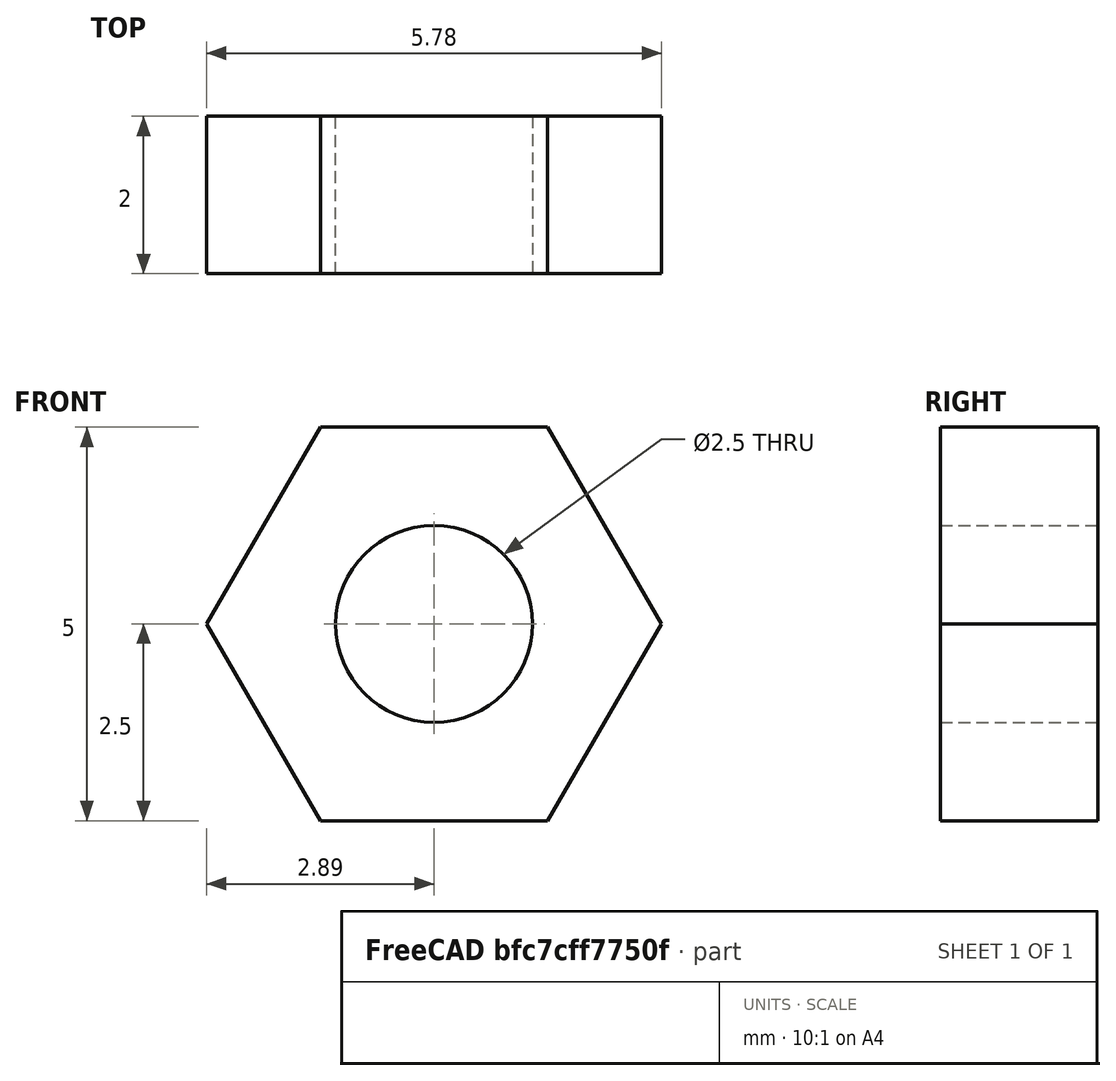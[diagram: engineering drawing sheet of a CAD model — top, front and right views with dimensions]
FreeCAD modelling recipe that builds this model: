
FCSTD DOCUMENT  (FreeCAD 0.20R29603 (Git))
Label: M2p5_moetrik
License: All rights reserved
LicenseURL: http://en.wikipedia.org/wiki/All_rights_reserved
objects: Sketcher::SketchObject×1, PartDesign::Pad×1, PartDesign::Body×1
note: 4 computed .brp shape members not serialized (recipe doc carries the construction recipe); baked Part::Feature solids carry a one-line shape summary decoded from their .brp

FEATURE [Sketcher::SketchObject] Sketch
  FullyConstrained = true
  MapMode = 5
  Placement = pos=(0,0,0) rot=(1,0,0;1.5708rad)
  Support = -> [XZ_Plane]
  sketch-geometry (8):
    g0: LineSegment StartX=1.44338 StartY=2.5 StartZ=0 EndX=-1.44338 EndY=2.5 EndZ=0
    g1: LineSegment StartX=-1.44338 StartY=2.5 StartZ=0 EndX=-2.88675 EndY=0 EndZ=0
    g2: LineSegment StartX=-2.88675 StartY=0 StartZ=0 EndX=-1.44338 EndY=-2.5 EndZ=0
    g3: LineSegment StartX=-1.44338 StartY=-2.5 StartZ=0 EndX=1.44338 EndY=-2.5 EndZ=0
    g4: LineSegment StartX=1.44338 StartY=-2.5 StartZ=0 EndX=2.88675 EndY=0 EndZ=0
    g5: LineSegment StartX=2.88675 StartY=0 StartZ=0 EndX=1.44338 EndY=2.5 EndZ=0
    g6: Circle CenterX=0 CenterY=0 CenterZ=0 NormalX=0 NormalY=0 NormalZ=1 AngleXU=0 Radius=2.88675
    g7: Circle CenterX=0 CenterY=0 CenterZ=0 NormalX=0 NormalY=0 NormalZ=1 AngleXU=0 Radius=1.25
  constraints (18):
    c: Coincident(g0,g1)
    c: Coincident(g1,g2)
    c: Coincident(g2,g3)
    c: Coincident(g3,g4)
    c: Coincident(g4,g5)
    c: Coincident(g5,g0)
    c: Equal(g0, g1-g5) x5
    c: PointOnObject(g0,g6)
    c: PointOnObject(g1,g6)
    c: PointOnObject(g2,g6)
    c: PointOnObject(g3,g6)
    c: PointOnObject(g4,g6)
    c: PointOnObject(g5,g6)
    c: Coincident(g6,g-1)
    c: Horizontal(g0)
    c: DistanceY(g3,g0) = 5
    c: Coincident(g7,g6)
    c: Diameter(g7) = 2.5
FEATURE [PartDesign::Pad] Pad
  Direction = (0,-1,2e-16)
  Length = 2
  Length2 = 10
  Placement = pos=(0,0,0) rot=(1,0,0;1.5708rad)
  Profile = -> Sketch
  ReferenceAxis = -> Sketch [N_Axis]
  Type = 0
FEATURE [PartDesign::Body] Body
  Group = -> [Sketch,Pad]
  Origin = -> Origin
  Tip = -> Pad
